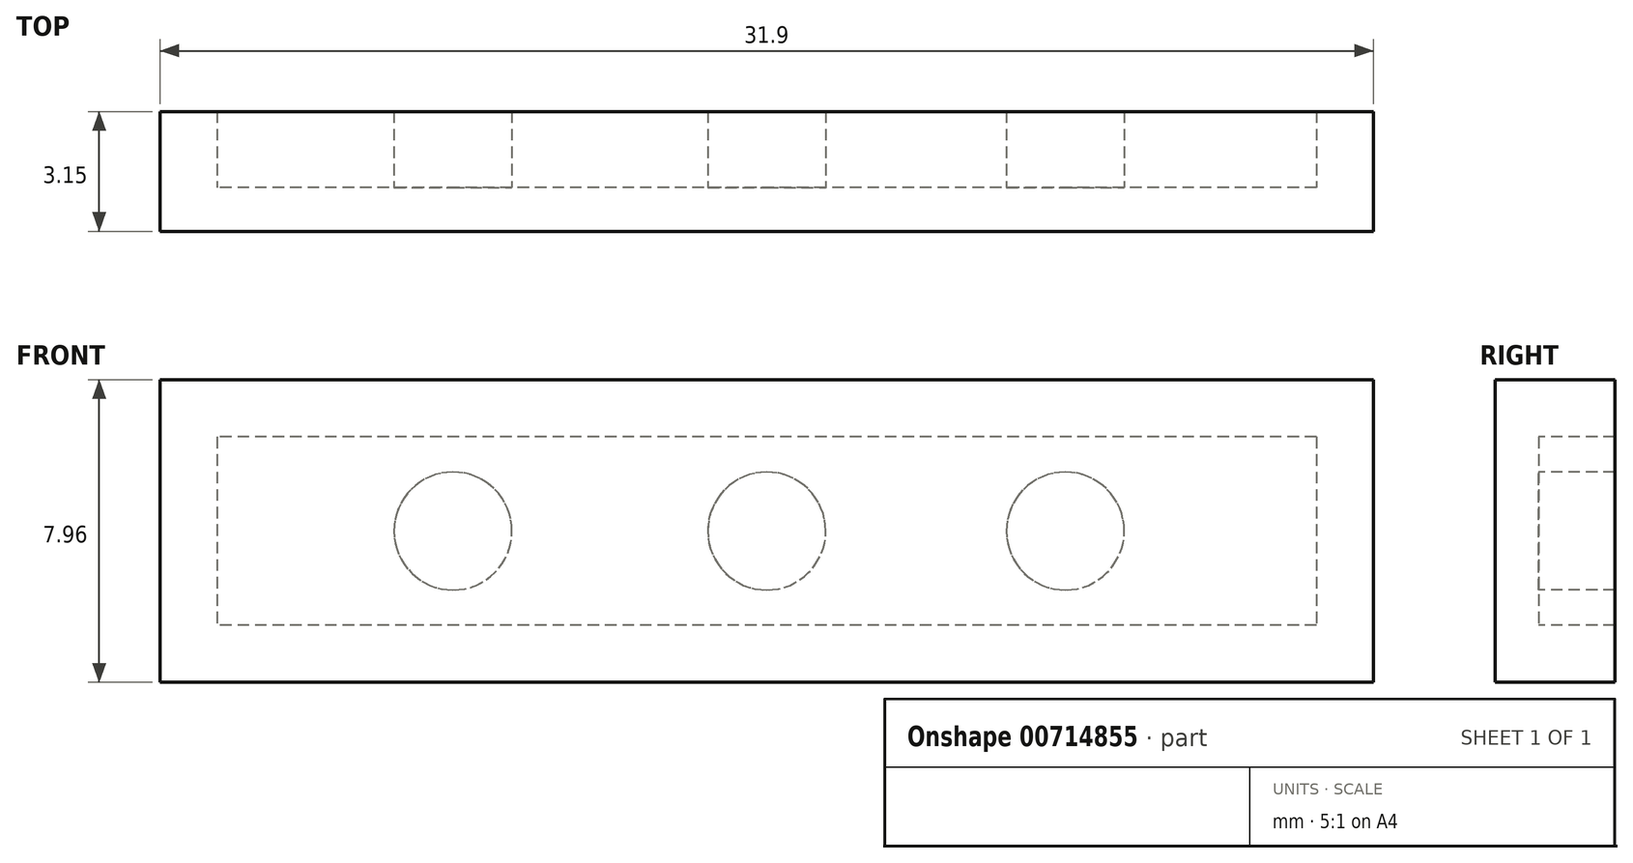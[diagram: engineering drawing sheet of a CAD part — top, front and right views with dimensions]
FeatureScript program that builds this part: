
annotation { "Feature Type Name" : "Feature", "Feature Type Description" : "" }
export const myFeature = defineFeature(function(context is Context, id is Id, definition is map)
    precondition{}
    {
        {
            var Q0;
            Q0=qCreatedBy(makeId("Front.planeOp"),FACE);
            var sketch = newSketch(context, id + "F0", { "sketchPlane" : qUnion([Q0])});
            skLineSegment(sketch, "E0.bottom", {"start": v(15.95, 3.97) * mm, "end": v(-15.95, 3.97) * mm});
            skLineSegment(sketch, "E0.top", {"start": v(15.95, -3.98) * mm, "end": v(-15.95, -3.98) * mm});
            skLineSegment(sketch, "E0.left", {"start": v(15.95, 3.97) * mm, "end": v(15.95, -3.98) * mm});
            skLineSegment(sketch, "E0.right", {"start": v(-15.95, 3.97) * mm, "end": v(-15.95, -3.98) * mm});
            skPoint(sketch, "E0.middle", {"position": v(0, 0) * mm});
            skSolve(sketch);
        }
        {
            var Q0;
            Q0 = qSketchRegion(id + "F0", true);
            extrude(context, id + "F1", {"entities" : qUnion([Q0]), "depth" : 1.15 * mm, "offsetDistance" : 25 * mm});
        }
        {
            var Q0;
            Q0=makeQuery(id+"F1.opExtrude","CAP_FACE",FACE,{"disambiguationData":[OSD([sQuery(id+"F0.wireOp",EDGE,"E0.bottom"),sQuery(id+"F0.wireOp",EDGE,"E0.top"),sQuery(id+"F0.wireOp",EDGE,"E0.left"),sQuery(id+"F0.wireOp",EDGE,"E0.right")])],"isStart":true});
            var sketch = newSketch(context, id + "F2", { "sketchPlane" : qUnion([Q0])});
            skLineSegment(sketch, "E1.bottom", {"start": v(-14.45, 2.47) * mm, "end": v(14.45, 2.47) * mm});
            skLineSegment(sketch, "E1.top", {"start": v(-14.45, -2.47) * mm, "end": v(14.45, -2.47) * mm});
            skLineSegment(sketch, "E1.left", {"start": v(-14.45, 2.47) * mm, "end": v(-14.45, -2.47) * mm});
            skLineSegment(sketch, "E1.right", {"start": v(14.45, 2.47) * mm, "end": v(14.45, -2.47) * mm});
            skPoint(sketch, "E1.middle", {"position": v(0, 0) * mm});
            skCircle(sketch, "E2", {"center": v(-7.85, 0) * mm, "radius": 1.55 * mm});
            skCircle(sketch, "E3", {"center": v(0, 0) * mm, "radius": 1.55 * mm});
            skCircle(sketch, "E4", {"center": v(8.25, 0) * mm, "radius": 1.55 * mm});
            skSolve(sketch);
        }
        {
            var Q0;
            Q0=makeQuery(id+"F2.imprint","IMPRINT",FACE,{"disambiguationData":[TD([[makeQuery(id+"F2.imprint","IMPRINT",EDGE,{"derivedFrom":sQuery(id+"F2.wireOp",EDGE,"E1.bottom")}),1.0]])]});
            var Q1;
            Q1=makeQuery(id+"F2.imprint","IMPRINT",FACE,{"disambiguationData":[TD([[makeQuery(id+"F2.imprint","IMPRINT",EDGE,{"derivedFrom":sQuery(id+"F2.wireOp",EDGE,"E2")}),1.0]])]});
            var Q2;
            Q2=makeQuery(id+"F2.imprint","IMPRINT",FACE,{"disambiguationData":[TD([[makeQuery(id+"F2.imprint","IMPRINT",EDGE,{"derivedFrom":sQuery(id+"F2.wireOp",EDGE,"E3")}),1.0]])]});
            var Q3;
            Q3=makeQuery(id+"F2.imprint","IMPRINT",FACE,{"disambiguationData":[TD([[makeQuery(id+"F2.imprint","IMPRINT",EDGE,{"derivedFrom":sQuery(id+"F2.wireOp",EDGE,"E4")}),1.0]])]});
            extrude(context, id + "F3", {"entities" : qUnion([Q0, Q1, Q2, Q3]), "operationType" : NewBodyOperationType.ADD, "depth" : 2 * mm, "offsetDistance" : 25 * mm});
        }
    });
